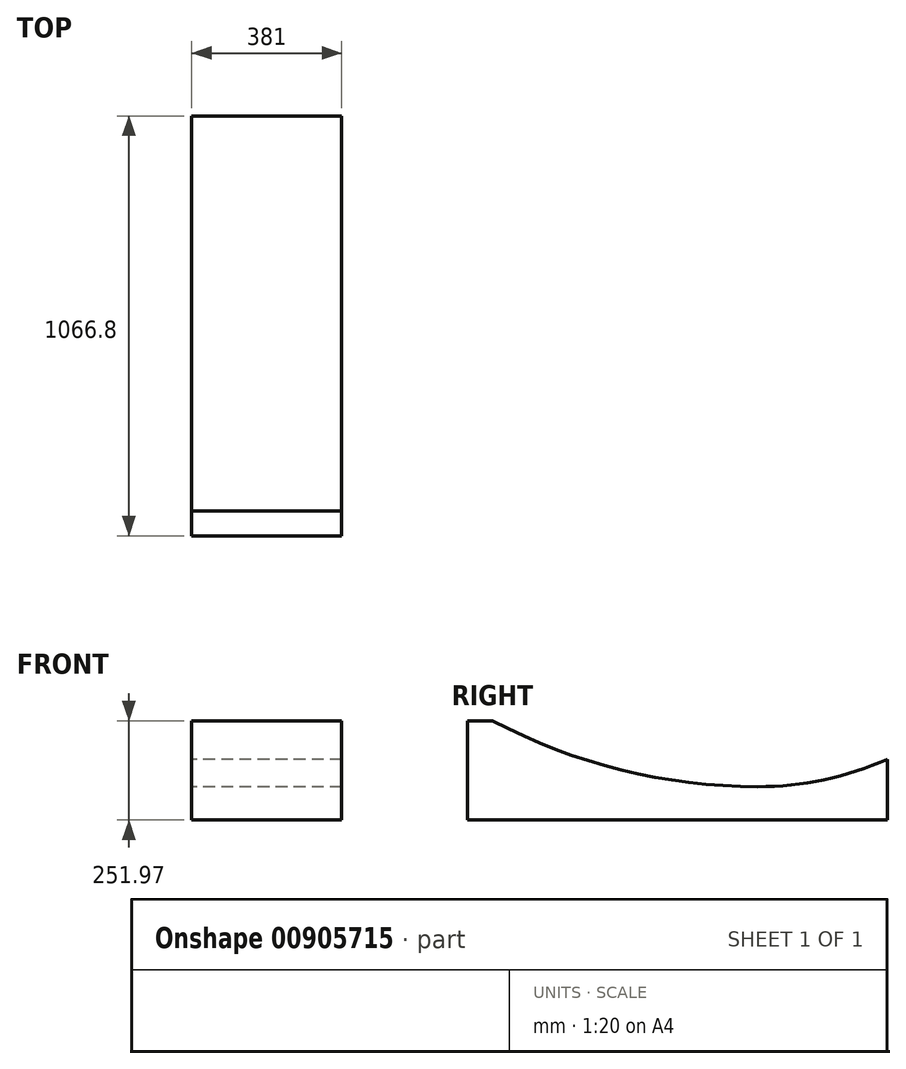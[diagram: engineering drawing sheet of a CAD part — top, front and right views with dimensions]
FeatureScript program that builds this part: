
annotation { "Feature Type Name" : "Feature", "Feature Type Description" : "" }
export const myFeature = defineFeature(function(context is Context, id is Id, definition is map)
    precondition{}
    {
        {
            var Q0;
            Q0=qCreatedBy(makeId("Right.planeOp"),FACE);
            var sketch = newSketch(context, id + "F0", { "sketchPlane" : qUnion([Q0])});
            skLineSegment(sketch, "E0.left", {"start": v(-59.03, 203.2) * mm, "end": v(-59.03, 0) * mm});
            skLineSegment(sketch, "E1.top", {"start": v(-59.03, -84.54) * mm, "end": v(1007.77, -84.54) * mm});
            skLineSegment(sketch, "E1.left", {"start": v(-59.03, 0) * mm, "end": v(-59.03, -84.54) * mm});
            skLineSegment(sketch, "E1.right", {"start": v(1007.77, 0) * mm, "end": v(1007.77, -84.54) * mm});
            skLineSegment(sketch, "E2", {"start": v(1007.77, 0) * mm, "end": v(1007.77, 69.85) * mm});
            skArc(sketch, "E3", {"start": v(-59.03, 203.2) * mm, "mid": v(295.52, 51.73) * mm, "end": v(677.57, 0) * mm});
            skArc(sketch, "E4", {"start": v(677.57, 0) * mm, "mid": v(846.33, 17.65) * mm, "end": v(1007.77, 69.85) * mm});
            skLineSegment(sketch, "E5", {"start": v(-59.03, 167.43) * mm, "end": v(4.47, 167.43) * mm});
            skSolve(sketch);
        }
        {
            var Q0;
            Q0=makeQuery(id+"F0.imprint","IMPRINT",FACE,{"disambiguationData":[TD([[makeQuery(id+"F0.imprint","IMPRINT",EDGE,{"derivedFrom":sQuery(id+"F0.wireOp",EDGE,"E1.top")}),1.0]])]});
            extrude(context, id + "F1", {"entities" : qUnion([Q0]), "depth" : 381 * mm, "offsetDistance" : 25.4 * mm});
        }
    });
